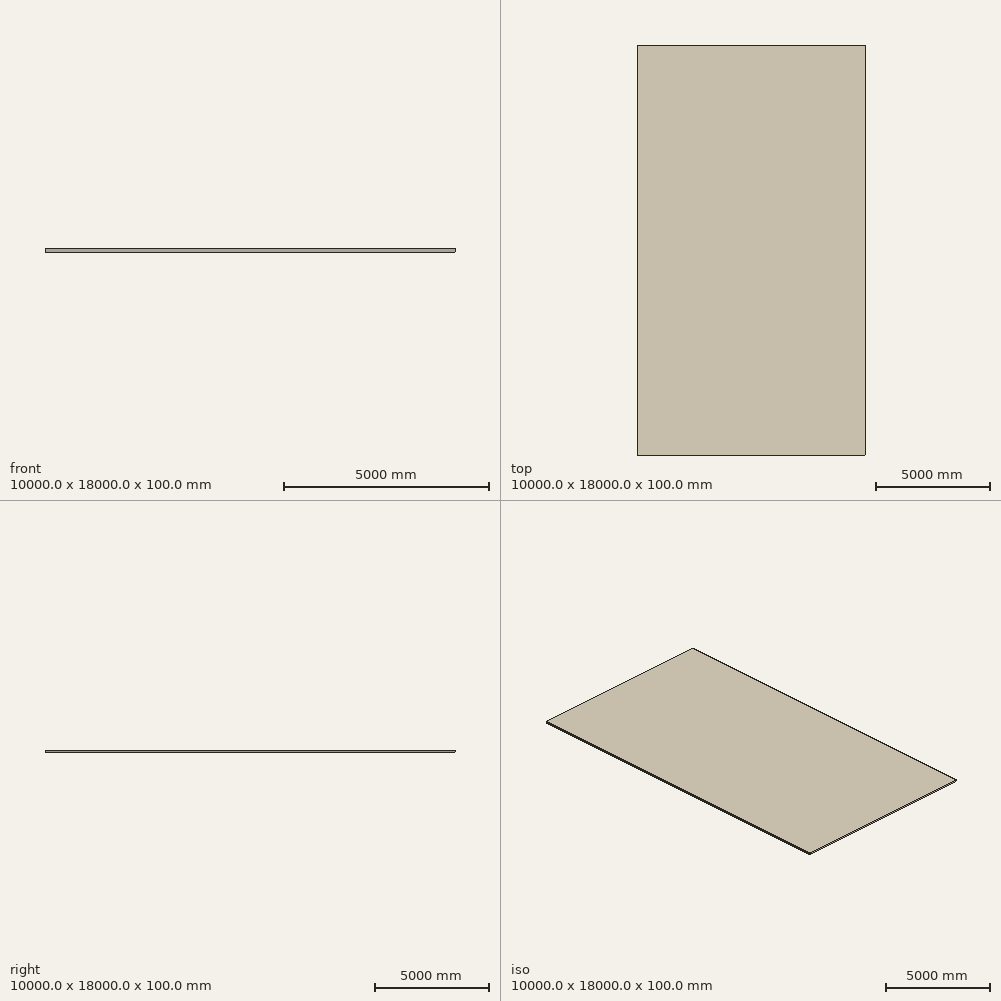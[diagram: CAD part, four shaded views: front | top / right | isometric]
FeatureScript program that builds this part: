
annotation { "Feature Type Name" : "Feature", "Feature Type Description" : "" }
export const myFeature = defineFeature(function(context is Context, id is Id, definition is map)
    precondition{}
    {
        {
            var Q0;
            Q0=qCreatedBy(makeId("Top.planeOp"),FACE);
            var sketch = newSketch(context, id + "F0", { "sketchPlane" : qUnion([Q0])});
            skLineSegment(sketch, "E0.bottom", {"start": v(-5000, 4000) * mm, "end": v(5000, 4000) * mm});
            skLineSegment(sketch, "E0.top", {"start": v(-5000, -14000) * mm, "end": v(5000, -14000) * mm});
            skLineSegment(sketch, "E0.left", {"start": v(-5000, 4000) * mm, "end": v(-5000, -14000) * mm});
            skLineSegment(sketch, "E0.right", {"start": v(5000, 4000) * mm, "end": v(5000, -14000) * mm});
            skPoint(sketch, "E0.middle", {"position": v(0, -5000) * mm});
            skSolve(sketch);
        }
        {
            var Q0;
            Q0=makeQuery(id+"F0.imprint","IMPRINT",FACE,{"disambiguationData":[TD([[makeQuery(id+"F0.imprint","IMPRINT",EDGE,{"derivedFrom":sQuery(id+"F0.wireOp",EDGE,"dMLpOUhB-4siO-7rh7-gh3J-v0ivMKi52hcK.bottom")}),-1.0]])]});
            var Q1;
            Q1=makeQuery(id+"F0.imprint","IMPRINT",FACE,{"disambiguationData":[TD([[makeQuery(id+"F0.imprint","IMPRINT",EDGE,{"derivedFrom":sQuery(id+"F0.wireOp",EDGE,"E0.bottom")}),-1.0]])]});
            extrude(context, id + "F1", {"entities" : qUnion([Q0, Q1]), "oppositeDirection" : true, "depth" : 100 * mm, "offsetDistance" : 25 * mm});
        }
    });
